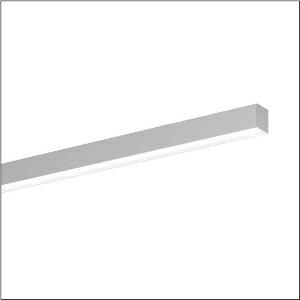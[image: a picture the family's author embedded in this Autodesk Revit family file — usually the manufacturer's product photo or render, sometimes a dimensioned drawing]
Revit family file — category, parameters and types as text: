
# Revit family: silica_r__21_51mx23tat4s_c658
name_source: partatom
category: Lighting Fixtures
units: mm (PartAtom-declared; Revit-internal decimal feet)

## family parameters
Cut with Voids When Loaded = No
Host = Face
Light Source = No
Part Type = Normal
Room Calculation Point = No
Round Connector Dimension = Use Diameter
Shared = No

## types (1)
- --- (1 x LED, 3230 lm, 32.4 W, 6500K)
    Apparent Load = 32 VA
    CIE Flux Codes = 78 96 99 100 100
    Color Rendering = 80
    Color Temperature = 6500K
    Default Elevation = 1800 mm
    Description = Silica® 21, office luminaire, primary optical cover: prismatic diffuser, of PMMA, CAT 2 (L<= 3000cd/m²), light emission: direct distribution, primary light characteristic: symmetric, installation type: surface-mounted, LED, rated luminous flux: 3.230lm, luminous efficacy: 95lm/W, light colour: 8tw, colour temperature: 2700..6500K, control gear: ECG DALI, with terminal, 3+2-pole, max. 2.5mm², mains connection: 220..240V, AC, 50/60Hz, rated input power: 34W, luminaire housing, of aluminium, metallic grey (RAL 9006), length: 1.204mm, width: 53mm, height: 53mm, protection rating (complete): IP20, insulation class (complete): insulation class I (protective earthing), certification: CE, permissible operating ambient temperature: 0..+35°C, standard: EN 50419, packaging unit: 1 piece
    Height = 0 mm  [stored 0 ft]
    Lamp = 1 x LED
    Lamp Light Flux = 3230 lm
    Lamp Power = 32.4 W
    Lamp count = 1
    Length = 1204 mm
    Luminous efficacy = 100 lm/W
    Manufacturer = Siteco
    ModVariant = No
    Model = 51MX23TAT4S
    Mounting Place = Ceiling
    Mounting Type = Recessed
    Number of Poles = 1
    OnlyDefault = Yes
    Power Factor = 1
    Product Name = Silica® 21
    Product group = office luminaire | ceiling recessed
    ProductGroupID = 401
    Protection Class = Protection class I
    Protection Degree = IP 20
    RLX_Detail_Level = 1
    RLX_Emergency_Light_Flux = 0 lm
    RLX_Emergency_Type = 0
    RLX_Emergency_Type_DB = No
    RlxData = <blob elided: 18029 chars, md5=49fc5e55>
    Socket = socket
    Standby Power = 0 W
    System Light Flux = 3230 lm
    System Power = 32 W
    Type Comments = individual setting
    Type Image = l_1313588.jpg
    URL = http://relux.com
    VarID = @adj_089169
    Voltage = 0 V
    Weight = 0.00 kg
    Width = 53 mm

note: [stored X ft] marks values corroborated as IEEE doubles in the binary element streams (Revit-internal decimal feet)

## geometry (parser evidence)
native form markers: Blend x4, Sweep x12
no freeform markers — native parametric forms only
